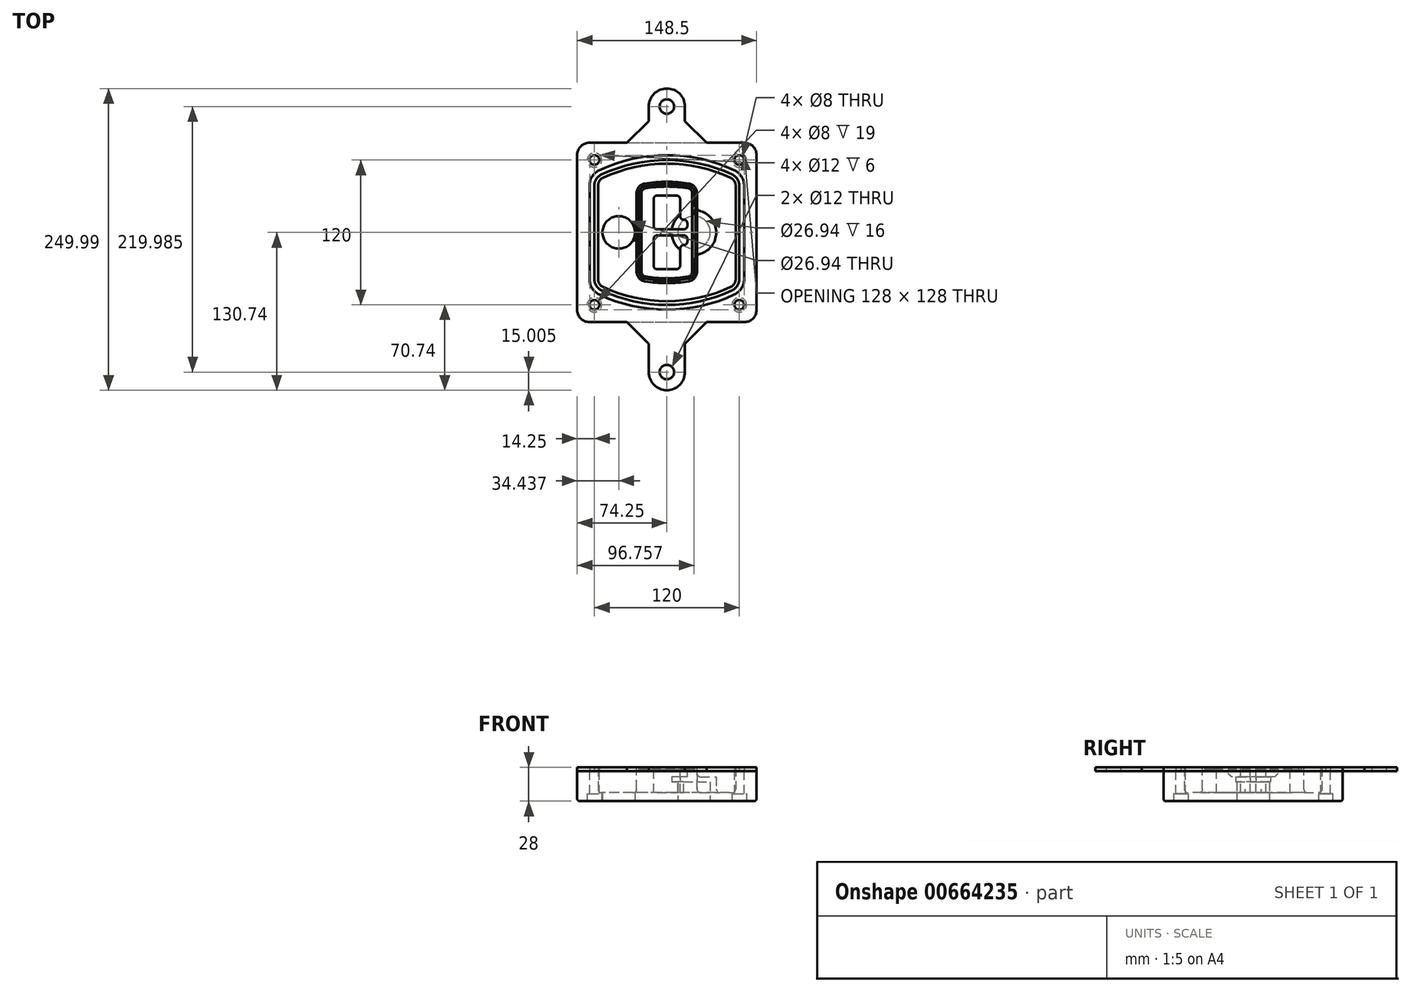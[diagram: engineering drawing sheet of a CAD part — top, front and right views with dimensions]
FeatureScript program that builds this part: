
annotation { "Feature Type Name" : "Feature", "Feature Type Description" : "" }
export const myFeature = defineFeature(function(context is Context, id is Id, definition is map)
    precondition{}
    {
        {
            var Q0;
            Q0=qCreatedBy(makeId("Top.planeOp"),FACE);
            var sketch = newSketch(context, id + "F0", { "sketchPlane" : qUnion([Q0])});
            skPoint(sketch, "E0.rect.middle", {"position": v(0, 0) * mm});
            skLineSegment(sketch, "E1.bottom", {"start": v(-64.25, -74.25) * mm, "end": v(64.25, -74.25) * mm});
            skLineSegment(sketch, "E1.top", {"start": v(-64.25, 74.25) * mm, "end": v(64.25, 74.25) * mm});
            skLineSegment(sketch, "E1.left", {"start": v(-74.25, -64.25) * mm, "end": v(-74.25, 64.25) * mm});
            skLineSegment(sketch, "E1.right", {"start": v(74.25, -64.25) * mm, "end": v(74.25, 64.25) * mm});
            skLineSegment(sketch, "E2", {"start": v(-74.25, 74.25) * mm, "end": v(74.25, -74.25) * mm, "construction": true});
            skLineSegment(sketch, "E3", {"start": v(74.25, 74.25) * mm, "end": v(-74.25, -74.25) * mm, "construction": true});
            skCircle(sketch, "E4", {"center": v(-60, 60) * mm, "radius": 4 * mm});
            skCircle(sketch, "E5", {"center": v(60, 60) * mm, "radius": 4 * mm});
            skCircle(sketch, "E6", {"center": v(60, -60) * mm, "radius": 4 * mm});
            skCircle(sketch, "E7", {"center": v(-60, -60) * mm, "radius": 4 * mm});
            skLineSegment(sketch, "E8", {"start": v(-60, 60) * mm, "end": v(60, 60) * mm, "construction": true});
            skLineSegment(sketch, "E9", {"start": v(60, 60) * mm, "end": v(60, -60) * mm, "construction": true});
            skLineSegment(sketch, "E10", {"start": v(60, -60) * mm, "end": v(-60, -60) * mm, "construction": true});
            skLineSegment(sketch, "E11", {"start": v(-60, -60) * mm, "end": v(-60, 60) * mm, "construction": true});
            skLineSegment(sketch, "E12", {"start": v(-60, 38.83) * mm, "end": v(-60, -38.83) * mm});
            skLineSegment(sketch, "E13", {"start": v(60, 38.83) * mm, "end": v(60, -38.83) * mm});
            skArc(sketch, "E14", {"start": v(54.26, 47.88) * mm, "mid": v(0, 60) * mm, "end": v(-54.26, 47.88) * mm});
            skArc(sketch, "E15", {"start": v(-54.26, -47.88) * mm, "mid": v(0, -60) * mm, "end": v(54.26, -47.88) * mm});
            skLineSegment(sketch, "E16", {"start": v(-60, 0) * mm, "end": v(60, 0) * mm, "construction": true});
            skPoint(sketch, "E17.visualSharp", {"position": v(-60, -45) * mm});
            skArc(sketch, "E17.filletArc", {"start": v(-60, -38.83) * mm, "mid": v(-58.44, -44.2) * mm, "end": v(-54.26, -47.88) * mm});
            skPoint(sketch, "E18.visualSharp", {"position": v(-60, 45) * mm});
            skArc(sketch, "E18.filletArc", {"start": v(-54.26, 47.88) * mm, "mid": v(-58.44, 44.2) * mm, "end": v(-60, 38.83) * mm});
            skPoint(sketch, "E19.visualSharp", {"position": v(60, 45) * mm});
            skArc(sketch, "E19.filletArc", {"start": v(60, 38.83) * mm, "mid": v(58.44, 44.2) * mm, "end": v(54.26, 47.88) * mm});
            skPoint(sketch, "E20.visualSharp", {"position": v(60, -45) * mm});
            skArc(sketch, "E20.filletArc", {"start": v(54.26, -47.88) * mm, "mid": v(58.44, -44.2) * mm, "end": v(60, -38.83) * mm});
            skPoint(sketch, "E21.visualSharp", {"position": v(-74.25, 74.25) * mm});
            skArc(sketch, "E21.filletArc", {"start": v(-64.25, 74.25) * mm, "mid": v(-71.32, 71.32) * mm, "end": v(-74.25, 64.25) * mm});
            skPoint(sketch, "E22.visualSharp", {"position": v(74.25, 74.25) * mm});
            skArc(sketch, "E22.filletArc", {"start": v(74.25, 64.25) * mm, "mid": v(71.32, 71.32) * mm, "end": v(64.25, 74.25) * mm});
            skPoint(sketch, "E23.visualSharp", {"position": v(74.25, -74.25) * mm});
            skArc(sketch, "E23.filletArc", {"start": v(64.25, -74.25) * mm, "mid": v(71.32, -71.32) * mm, "end": v(74.25, -64.25) * mm});
            skPoint(sketch, "E24.visualSharp", {"position": v(-74.25, -74.25) * mm});
            skArc(sketch, "E24.filletArc", {"start": v(-74.25, -64.25) * mm, "mid": v(-71.32, -71.32) * mm, "end": v(-64.25, -74.25) * mm});
            skArc(sketch, "E25.0", {"start": v(57, 38.83) * mm, "mid": v(55.9, 42.58) * mm, "end": v(52.98, 45.17) * mm});
            skLineSegment(sketch, "E25.1", {"start": v(57, 38.83) * mm, "end": v(57, -38.83) * mm});
            skArc(sketch, "E25.2", {"start": v(52.98, -45.17) * mm, "mid": v(55.9, -42.58) * mm, "end": v(57, -38.83) * mm});
            skArc(sketch, "E25.3", {"start": v(-52.98, -45.17) * mm, "mid": v(0, -57) * mm, "end": v(52.98, -45.17) * mm});
            skArc(sketch, "E25.4", {"start": v(-57, -38.83) * mm, "mid": v(-55.9, -42.58) * mm, "end": v(-52.98, -45.17) * mm});
            skArc(sketch, "E25.5", {"start": v(52.98, 45.17) * mm, "mid": v(0, 57) * mm, "end": v(-52.98, 45.17) * mm});
            skLineSegment(sketch, "E25.6", {"start": v(-57, 38.83) * mm, "end": v(-57, -38.83) * mm});
            skArc(sketch, "E25.7", {"start": v(-52.98, 45.17) * mm, "mid": v(-55.9, 42.58) * mm, "end": v(-57, 38.83) * mm});
            skArc(sketch, "E26.0", {"start": v(-55.96, 51.5) * mm, "mid": v(-61.82, 46.33) * mm, "end": v(-64, 38.83) * mm});
            skArc(sketch, "E26.1", {"start": v(55.96, 51.5) * mm, "mid": v(0, 64) * mm, "end": v(-55.96, 51.5) * mm});
            skArc(sketch, "E26.2", {"start": v(64, 38.83) * mm, "mid": v(61.82, 46.33) * mm, "end": v(55.96, 51.5) * mm});
            skLineSegment(sketch, "E26.3", {"start": v(64, 38.83) * mm, "end": v(64, -38.83) * mm});
            skArc(sketch, "E26.4", {"start": v(55.96, -51.5) * mm, "mid": v(61.82, -46.33) * mm, "end": v(64, -38.83) * mm});
            skLineSegment(sketch, "E26.5", {"start": v(-64, 38.83) * mm, "end": v(-64, -38.83) * mm});
            skArc(sketch, "E26.6", {"start": v(-55.96, -51.5) * mm, "mid": v(0, -64) * mm, "end": v(55.96, -51.5) * mm});
            skArc(sketch, "E26.7", {"start": v(-64, -38.83) * mm, "mid": v(-61.82, -46.33) * mm, "end": v(-55.96, -51.5) * mm});
            skLineSegment(sketch, "E27", {"start": v(0, 74.25) * mm, "end": v(0, 104.25) * mm, "construction": true});
            skCircle(sketch, "E28", {"center": v(0, 104.25) * mm, "radius": 6 * mm});
            skArc(sketch, "E29", {"start": v(-15, 104.25) * mm, "mid": v(0, 119.25) * mm, "end": v(15, 104.25) * mm});
            skLineSegment(sketch, "E30", {"start": v(-15, 104.25) * mm, "end": v(-15, 92.25) * mm});
            skLineSegment(sketch, "E31", {"start": v(15, 104.25) * mm, "end": v(15, 92.25) * mm});
            skLineSegment(sketch, "E32", {"start": v(15, 92.25) * mm, "end": v(33, 74.25) * mm});
            skLineSegment(sketch, "E33", {"start": v(-15, 92.25) * mm, "end": v(-33, 74.25) * mm});
            skArc(sketch, "E34.MirrorCS", {"start": v(15, 104.25) * mm, "mid": v(0, 119.25) * mm, "end": v(-15, 104.25) * mm});
            skLineSegment(sketch, "E35", {"start": v(-33, -74.25) * mm, "end": v(-15, -92.25) * mm});
            skLineSegment(sketch, "E36", {"start": v(33, -74.25) * mm, "end": v(15, -92.25) * mm});
            skLineSegment(sketch, "E37", {"start": v(-15, -92.25) * mm, "end": v(-15, -115.74) * mm});
            skLineSegment(sketch, "E38", {"start": v(15, -92.25) * mm, "end": v(15, -115.74) * mm});
            skCircle(sketch, "E39", {"center": v(0, -115.74) * mm, "radius": 6 * mm});
            skArc(sketch, "E40", {"start": v(-15, -115.74) * mm, "mid": v(0, -130.74) * mm, "end": v(15, -115.74) * mm});
            skSolve(sketch);
        }
        {
            var Q0;
            Q0=makeQuery(id+"F0.imprint","IMPRINT",FACE,{"disambiguationData":[TD([[makeQuery(id+"F0.imprint","IMPRINT",EDGE,{"derivedFrom":sQuery(id+"F0.wireOp",EDGE,"E1.bottom")}),1.0]])]});
            var Q1;
            Q1=makeQuery(id+"F0.imprint","IMPRINT",FACE,{"disambiguationData":[TD([[makeQuery(id+"F0.imprint","IMPRINT",EDGE,{"derivedFrom":sQuery(id+"F0.wireOp",EDGE,"E12")}),1.0]])]});
            var Q2;
            Q2=makeQuery(id+"F0.imprint","IMPRINT",FACE,{"disambiguationData":[TD([[makeQuery(id+"F0.imprint","IMPRINT",EDGE,{"derivedFrom":sQuery(id+"F0.wireOp",EDGE,"E25.0")}),1.0]])]});
            var Q3;
            Q3=makeQuery(id+"F0.imprint","IMPRINT",FACE,{"disambiguationData":[TD([[makeQuery(id+"F0.imprint","IMPRINT",EDGE,{"derivedFrom":sQuery(id+"F0.wireOp",EDGE,"E12")}),-1.0]])]});
            extrude(context, id + "F1", {"entities" : qUnion([Q0, Q1, Q2, Q3]), "oppositeDirection" : true, "depth" : 25 * mm});
        }
        {
            var Q0;
            Q0=makeQuery(id+"F0.imprint","IMPRINT",FACE,{"disambiguationData":[TD([[makeQuery(id+"F0.imprint","IMPRINT",EDGE,{"derivedFrom":sQuery(id+"F0.wireOp",EDGE,"E12")}),1.0]])]});
            extrude(context, id + "F2", {"entities" : qUnion([Q0]), "operationType" : NewBodyOperationType.ADD, "depth" : 3 * mm});
        }
        {
            var Q0;
            Q0=makeQuery(id+"F0.imprint","IMPRINT",FACE,{"disambiguationData":[TD([[makeQuery(id+"F0.imprint","IMPRINT",EDGE,{"derivedFrom":sQuery(id+"F0.wireOp",EDGE,"E25.0")}),1.0]])]});
            extrude(context, id + "F3", {"entities" : qUnion([Q0]), "operationType" : NewBodyOperationType.REMOVE, "oppositeDirection" : true, "depth" : 18 * mm});
        }
        {
            var Q0;
            Q0=makeQuery(id+"F2.opExtrude","CAP_FACE",FACE,{"disambiguationData":[OSD([sQuery(id+"F0.wireOp",EDGE,"E12"),sQuery(id+"F0.wireOp",EDGE,"E13"),sQuery(id+"F0.wireOp",EDGE,"E14"),sQuery(id+"F0.wireOp",EDGE,"E15"),sQuery(id+"F0.wireOp",EDGE,"E17.filletArc"),sQuery(id+"F0.wireOp",EDGE,"E18.filletArc"),sQuery(id+"F0.wireOp",EDGE,"E19.filletArc"),sQuery(id+"F0.wireOp",EDGE,"E20.filletArc"),sQuery(id+"F0.wireOp",EDGE,"E25.0"),sQuery(id+"F0.wireOp",EDGE,"E25.1"),sQuery(id+"F0.wireOp",EDGE,"E25.2"),sQuery(id+"F0.wireOp",EDGE,"E25.3"),sQuery(id+"F0.wireOp",EDGE,"E25.4"),sQuery(id+"F0.wireOp",EDGE,"E25.5"),sQuery(id+"F0.wireOp",EDGE,"E25.6"),sQuery(id+"F0.wireOp",EDGE,"E25.7")])],"isStart":false});
            var sketch = newSketch(context, id + "F4", { "sketchPlane" : qUnion([Q0])});
            skArc(sketch, "E41.0", {"start": v(-18.34, -40.45) * mm, "mid": v(0, -42) * mm, "end": v(18.34, -40.45) * mm});
            skArc(sketch, "E42.0", {"start": v(18.34, 40.45) * mm, "mid": v(0, 42) * mm, "end": v(-18.34, 40.45) * mm});
            skLineSegment(sketch, "E43", {"start": v(-25, 32.57) * mm, "end": v(-25, -32.57) * mm});
            skLineSegment(sketch, "E44", {"start": v(25, 32.57) * mm, "end": v(25, -32.57) * mm});
            skLineSegment(sketch, "E45", {"start": v(-25, 39.1) * mm, "end": v(25, 39.1) * mm, "construction": true});
            skLineSegment(sketch, "E46", {"start": v(-25, -39.1) * mm, "end": v(25, -39.1) * mm, "construction": true});
            skPoint(sketch, "E47.visualSharp", {"position": v(-25, 39.1) * mm});
            skArc(sketch, "E47.filletArc", {"start": v(-18.34, 40.45) * mm, "mid": v(-23.11, 37.73) * mm, "end": v(-25, 32.57) * mm});
            skPoint(sketch, "E48.visualSharp", {"position": v(25, 39.1) * mm});
            skArc(sketch, "E48.filletArc", {"start": v(25, 32.57) * mm, "mid": v(23.11, 37.73) * mm, "end": v(18.34, 40.45) * mm});
            skPoint(sketch, "E49.visualSharp", {"position": v(25, -39.1) * mm});
            skArc(sketch, "E49.filletArc", {"start": v(18.34, -40.45) * mm, "mid": v(23.11, -37.73) * mm, "end": v(25, -32.57) * mm});
            skPoint(sketch, "E50.visualSharp", {"position": v(-25, -39.1) * mm});
            skArc(sketch, "E50.filletArc", {"start": v(-25, -32.57) * mm, "mid": v(-23.11, -37.73) * mm, "end": v(-18.34, -40.45) * mm});
            skArc(sketch, "E51.0", {"start": v(52.98, 45.17) * mm, "mid": v(0, 57) * mm, "end": v(-52.98, 45.17) * mm});
            skArc(sketch, "E51.1", {"start": v(-52.98, 45.17) * mm, "mid": v(-55.9, 42.58) * mm, "end": v(-57, 38.83) * mm});
            skLineSegment(sketch, "E51.2", {"start": v(-57, 38.83) * mm, "end": v(-57, -38.83) * mm});
            skArc(sketch, "E51.3", {"start": v(-57, -38.83) * mm, "mid": v(-55.9, -42.58) * mm, "end": v(-52.98, -45.17) * mm});
            skArc(sketch, "E51.4", {"start": v(-52.98, -45.17) * mm, "mid": v(0, -57) * mm, "end": v(52.98, -45.17) * mm});
            skArc(sketch, "E51.5", {"start": v(52.98, -45.17) * mm, "mid": v(55.9, -42.58) * mm, "end": v(57, -38.83) * mm});
            skLineSegment(sketch, "E51.6", {"start": v(57, 38.83) * mm, "end": v(57, -38.83) * mm});
            skArc(sketch, "E51.7", {"start": v(57, 38.83) * mm, "mid": v(55.9, 42.58) * mm, "end": v(52.98, 45.17) * mm});
            skLineSegment(sketch, "E52.0", {"start": v(23, 32.57) * mm, "end": v(23, -32.57) * mm});
            skArc(sketch, "E52.1", {"start": v(18, -38.48) * mm, "mid": v(21.58, -36.44) * mm, "end": v(23, -32.57) * mm});
            skArc(sketch, "E52.2", {"start": v(-18, -38.48) * mm, "mid": v(0, -40) * mm, "end": v(18, -38.48) * mm});
            skArc(sketch, "E52.3", {"start": v(-23, -32.57) * mm, "mid": v(-21.58, -36.44) * mm, "end": v(-18, -38.48) * mm});
            skLineSegment(sketch, "E52.4", {"start": v(-23, 32.57) * mm, "end": v(-23, -32.57) * mm});
            skArc(sketch, "E52.5", {"start": v(23, 32.57) * mm, "mid": v(21.58, 36.44) * mm, "end": v(18, 38.48) * mm});
            skArc(sketch, "E52.6", {"start": v(-18, 38.48) * mm, "mid": v(-21.58, 36.44) * mm, "end": v(-23, 32.57) * mm});
            skArc(sketch, "E52.7", {"start": v(18, 38.48) * mm, "mid": v(0, 40) * mm, "end": v(-18, 38.48) * mm});
            skArc(sketch, "E53.0", {"start": v(21, 32.57) * mm, "mid": v(20.06, 35.15) * mm, "end": v(17.67, 36.5) * mm});
            skLineSegment(sketch, "E53.1", {"start": v(21, 32.57) * mm, "end": v(21, -32.57) * mm});
            skArc(sketch, "E53.2", {"start": v(17.67, -36.5) * mm, "mid": v(20.06, -35.15) * mm, "end": v(21, -32.57) * mm});
            skArc(sketch, "E53.3", {"start": v(-17.67, -36.5) * mm, "mid": v(0, -38) * mm, "end": v(17.67, -36.5) * mm});
            skArc(sketch, "E53.4", {"start": v(-21, -32.57) * mm, "mid": v(-20.06, -35.15) * mm, "end": v(-17.67, -36.5) * mm});
            skArc(sketch, "E53.5", {"start": v(17.67, 36.5) * mm, "mid": v(0, 38) * mm, "end": v(-17.67, 36.5) * mm});
            skLineSegment(sketch, "E53.6", {"start": v(-21, 32.57) * mm, "end": v(-21, -32.57) * mm});
            skArc(sketch, "E53.7", {"start": v(-17.67, 36.5) * mm, "mid": v(-20.06, 35.15) * mm, "end": v(-21, 32.57) * mm});
            skLineSegment(sketch, "E54", {"start": v(-25, 0) * mm, "end": v(25, 0) * mm, "construction": true});
            skLineSegment(sketch, "E55", {"start": v(-11, 5.5) * mm, "end": v(-11, 27.5) * mm});
            skLineSegment(sketch, "E56", {"start": v(-8, 30.5) * mm, "end": v(8, 30.5) * mm});
            skLineSegment(sketch, "E57", {"start": v(11, 27.5) * mm, "end": v(11, 13.5) * mm});
            skLineSegment(sketch, "E58", {"start": v(14, 10.5) * mm, "end": v(14, 10.5) * mm});
            skLineSegment(sketch, "E59", {"start": v(17, 7.5) * mm, "end": v(17, 5.5) * mm});
            skLineSegment(sketch, "E60", {"start": v(14, 2.5) * mm, "end": v(-8, 2.5) * mm});
            skPoint(sketch, "E61.visualSharp", {"position": v(-11, 30.5) * mm});
            skArc(sketch, "E61.filletArc", {"start": v(-8, 30.5) * mm, "mid": v(-10.12, 29.62) * mm, "end": v(-11, 27.5) * mm});
            skPoint(sketch, "E62.visualSharp", {"position": v(11, 30.5) * mm});
            skArc(sketch, "E62.filletArc", {"start": v(11, 27.5) * mm, "mid": v(10.12, 29.62) * mm, "end": v(8, 30.5) * mm});
            skPoint(sketch, "E63.visualSharp", {"position": v(11, 10.5) * mm});
            skArc(sketch, "E63.filletArc", {"start": v(11, 13.5) * mm, "mid": v(11.88, 11.38) * mm, "end": v(14, 10.5) * mm});
            skPoint(sketch, "E64.visualSharp", {"position": v(17, 10.5) * mm});
            skArc(sketch, "E64.filletArc", {"start": v(17, 7.5) * mm, "mid": v(16.12, 9.62) * mm, "end": v(14, 10.5) * mm});
            skPoint(sketch, "E65.visualSharp", {"position": v(17, 2.5) * mm});
            skArc(sketch, "E65.filletArc", {"start": v(14, 2.5) * mm, "mid": v(16.12, 3.38) * mm, "end": v(17, 5.5) * mm});
            skPoint(sketch, "E66.visualSharp", {"position": v(-11, 2.5) * mm});
            skArc(sketch, "E66.filletArc", {"start": v(-11, 5.5) * mm, "mid": v(-10.12, 3.38) * mm, "end": v(-8, 2.5) * mm});
            skLineSegment(sketch, "E67.0.MirrorCS", {"start": v(14, -2.5) * mm, "end": v(-8, -2.5) * mm});
            skArc(sketch, "E68.0.MirrorCS", {"start": v(-11, -5.5) * mm, "mid": v(-10.12, -3.38) * mm, "end": v(-8, -2.5) * mm});
            skLineSegment(sketch, "E69.0.MirrorCS", {"start": v(-11, -5.5) * mm, "end": v(-11, -27.5) * mm});
            skArc(sketch, "E70.0.MirrorCS", {"start": v(-8, -30.5) * mm, "mid": v(-10.12, -29.62) * mm, "end": v(-11, -27.5) * mm});
            skLineSegment(sketch, "E71.0.MirrorCS", {"start": v(-8, -30.5) * mm, "end": v(8, -30.5) * mm});
            skArc(sketch, "E72.0.MirrorCS", {"start": v(11, -27.5) * mm, "mid": v(10.12, -29.62) * mm, "end": v(8, -30.5) * mm});
            skLineSegment(sketch, "E73.0.MirrorCS", {"start": v(11, -27.5) * mm, "end": v(11, -13.5) * mm});
            skArc(sketch, "E74.0.MirrorCS", {"start": v(11, -13.5) * mm, "mid": v(11.88, -11.38) * mm, "end": v(14, -10.5) * mm});
            skArc(sketch, "E75.0.MirrorCS", {"start": v(17, -7.5) * mm, "mid": v(16.12, -9.62) * mm, "end": v(14, -10.5) * mm});
            skLineSegment(sketch, "E76.0.MirrorCS", {"start": v(17, -7.5) * mm, "end": v(17, -5.5) * mm});
            skArc(sketch, "E77.0.MirrorCS", {"start": v(14, -2.5) * mm, "mid": v(16.12, -3.38) * mm, "end": v(17, -5.5) * mm});
            skSolve(sketch);
        }
        {
            var Q0;
            Q0=makeQuery(id+"F4.imprint","IMPRINT",FACE,{"disambiguationData":[TD([[makeQuery(id+"F4.imprint","IMPRINT",EDGE,{"derivedFrom":sQuery(id+"F4.wireOp",EDGE,"E41.0")}),1.0]])]});
            var Q1;
            Q1=makeQuery(id+"F4.imprint","IMPRINT",FACE,{"disambiguationData":[TD([[makeQuery(id+"F4.imprint","IMPRINT",EDGE,{"derivedFrom":sQuery(id+"F4.wireOp",EDGE,"E52.0")}),-1.0]])]});
            var Q2;
            Q2=makeQuery(id+"F4.imprint","IMPRINT",FACE,{"disambiguationData":[TD([[makeQuery(id+"F4.imprint","IMPRINT",EDGE,{"derivedFrom":sQuery(id+"F4.wireOp",EDGE,"E53.0")}),1.0]])]});
            extrude(context, id + "F5", {"entities" : qUnion([Q0, Q1, Q2]), "operationType" : NewBodyOperationType.ADD, "endBound" : BoundingType.UP_TO_NEXT, "oppositeDirection" : true, "depth" : 25 * mm});
        }
        {
            var Q0;
            Q0=makeQuery(id+"F4.imprint","IMPRINT",FACE,{"disambiguationData":[TD([[makeQuery(id+"F4.imprint","IMPRINT",EDGE,{"derivedFrom":sQuery(id+"F4.wireOp",EDGE,"E52.0")}),-1.0]])]});
            extrude(context, id + "F6", {"entities" : qUnion([Q0]), "operationType" : NewBodyOperationType.REMOVE, "oppositeDirection" : true, "depth" : 2 * mm});
        }
        {
            var Q0;
            Q0=makeQuery(id+"F1.opExtrude","CAP_FACE",FACE,{"disambiguationData":[OSD([sQuery(id+"F0.wireOp",EDGE,"E1.bottom"),sQuery(id+"F0.wireOp",EDGE,"E1.top"),sQuery(id+"F0.wireOp",EDGE,"E1.left"),sQuery(id+"F0.wireOp",EDGE,"E1.right"),sQuery(id+"F0.wireOp",EDGE,"E4"),sQuery(id+"F0.wireOp",EDGE,"E5"),sQuery(id+"F0.wireOp",EDGE,"E6"),sQuery(id+"F0.wireOp",EDGE,"E7"),sQuery(id+"F0.wireOp",EDGE,"E21.filletArc"),sQuery(id+"F0.wireOp",EDGE,"E22.filletArc"),sQuery(id+"F0.wireOp",EDGE,"E23.filletArc"),sQuery(id+"F0.wireOp",EDGE,"E24.filletArc")])],"isStart":false});
            var sketch = newSketch(context, id + "F7", { "sketchPlane" : qUnion([Q0])});
            skCircle(sketch, "E78", {"center": v(22.5, 0) * mm, "radius": 13.47 * mm});
            skCircle(sketch, "E79", {"center": v(-39.81, 0) * mm, "radius": 13.47 * mm});
            skLineSegment(sketch, "E80", {"start": v(74.25, 0) * mm, "end": v(-74.25, 0) * mm});
            skCircle(sketch, "E81", {"center": v(22.5, 0) * mm, "radius": 18.47 * mm});
            skCircle(sketch, "E82", {"center": v(60, -60) * mm, "radius": 6 * mm});
            skCircle(sketch, "E83", {"center": v(-60, -60) * mm, "radius": 6 * mm});
            skCircle(sketch, "E84", {"center": v(-60, 60) * mm, "radius": 6 * mm});
            skCircle(sketch, "E85", {"center": v(60, 60) * mm, "radius": 6 * mm});
            skSolve(sketch);
        }
        {
            var Q0;
            {var subQ1=sQuery(id+"F7.wireOp",EDGE,"E80");var subQ4=sQuery(id+"F7.wireOp",EDGE,"E78");var subQ6=makeQuery(id+"F7.imprint","INTERSECT",VERTEX,{"disambiguationData":[OD(0.0)],"derivedFrom":[subQ4,subQ1]});Q0=makeQuery(id+"F7.imprint","IMPRINT",FACE,{"disambiguationData":[TD([[makeQuery(id+"F7.imprint","IMPRINT",EDGE,{"disambiguationData":[TD([[subQ6,-1.0]])],"derivedFrom":subQ4}),-1.0]])]});}
            var Q1;
            {var subQ0=sQuery(id+"F7.wireOp",EDGE,"E80");var subQ1=sQuery(id+"F7.wireOp",EDGE,"E78");var subQ3=makeQuery(id+"F7.imprint","INTERSECT",VERTEX,{"disambiguationData":[OD(0.0)],"derivedFrom":[subQ1,subQ0]});Q1=makeQuery(id+"F7.imprint","IMPRINT",FACE,{"disambiguationData":[TD([[makeQuery(id+"F7.imprint","IMPRINT",EDGE,{"disambiguationData":[TD([[subQ3,-1.0]])],"derivedFrom":subQ1}),1.0]])]});}
            var Q2;
            {var subQ0=sQuery(id+"F7.wireOp",EDGE,"E80");var subQ1=sQuery(id+"F7.wireOp",EDGE,"E78");var subQ3=makeQuery(id+"F7.imprint","INTERSECT",VERTEX,{"disambiguationData":[OD(0.0)],"derivedFrom":[subQ1,subQ0]});Q2=makeQuery(id+"F7.imprint","IMPRINT",FACE,{"disambiguationData":[TD([[makeQuery(id+"F7.imprint","IMPRINT",EDGE,{"disambiguationData":[TD([[subQ3,1.0]])],"derivedFrom":subQ1}),1.0]])]});}
            var Q3;
            {var subQ1=sQuery(id+"F7.wireOp",EDGE,"E80");var subQ4=sQuery(id+"F7.wireOp",EDGE,"E78");var subQ6=makeQuery(id+"F7.imprint","INTERSECT",VERTEX,{"disambiguationData":[OD(0.0)],"derivedFrom":[subQ4,subQ1]});Q3=makeQuery(id+"F7.imprint","IMPRINT",FACE,{"disambiguationData":[TD([[makeQuery(id+"F7.imprint","IMPRINT",EDGE,{"disambiguationData":[TD([[subQ6,1.0]])],"derivedFrom":subQ4}),-1.0]])]});}
            extrude(context, id + "F8", {"entities" : qUnion([Q0, Q1, Q2, Q3]), "operationType" : NewBodyOperationType.ADD, "oppositeDirection" : true, "depth" : 20 * mm});
        }
        {
            var Q0;
            {var subQ0=sQuery(id+"F7.wireOp",EDGE,"E80");var subQ1=sQuery(id+"F7.wireOp",EDGE,"E78");var subQ3=makeQuery(id+"F7.imprint","INTERSECT",VERTEX,{"disambiguationData":[OD(0.0)],"derivedFrom":[subQ1,subQ0]});Q0=makeQuery(id+"F7.imprint","IMPRINT",FACE,{"disambiguationData":[TD([[makeQuery(id+"F7.imprint","IMPRINT",EDGE,{"disambiguationData":[TD([[subQ3,-1.0]])],"derivedFrom":subQ1}),1.0]])]});}
            var Q1;
            {var subQ0=sQuery(id+"F7.wireOp",EDGE,"E80");var subQ1=sQuery(id+"F7.wireOp",EDGE,"E78");var subQ3=makeQuery(id+"F7.imprint","INTERSECT",VERTEX,{"disambiguationData":[OD(0.0)],"derivedFrom":[subQ1,subQ0]});Q1=makeQuery(id+"F7.imprint","IMPRINT",FACE,{"disambiguationData":[TD([[makeQuery(id+"F7.imprint","IMPRINT",EDGE,{"disambiguationData":[TD([[subQ3,1.0]])],"derivedFrom":subQ1}),1.0]])]});}
            extrude(context, id + "F9", {"entities" : qUnion([Q0, Q1]), "operationType" : NewBodyOperationType.REMOVE, "oppositeDirection" : true, "depth" : 16 * mm});
        }
        {
            var Q0;
            {var subQ0=sQuery(id+"F7.wireOp",EDGE,"E80");var subQ1=sQuery(id+"F7.wireOp",EDGE,"E79");var subQ3=makeQuery(id+"F7.imprint","INTERSECT",VERTEX,{"disambiguationData":[OD(0.0)],"derivedFrom":[subQ1,subQ0]});Q0=makeQuery(id+"F7.imprint","IMPRINT",FACE,{"disambiguationData":[TD([[makeQuery(id+"F7.imprint","IMPRINT",EDGE,{"disambiguationData":[TD([[subQ3,-1.0]])],"derivedFrom":subQ1}),1.0]])]});}
            var Q1;
            {var subQ0=sQuery(id+"F7.wireOp",EDGE,"E80");var subQ1=sQuery(id+"F7.wireOp",EDGE,"E79");var subQ3=makeQuery(id+"F7.imprint","INTERSECT",VERTEX,{"disambiguationData":[OD(0.0)],"derivedFrom":[subQ1,subQ0]});Q1=makeQuery(id+"F7.imprint","IMPRINT",FACE,{"disambiguationData":[TD([[makeQuery(id+"F7.imprint","IMPRINT",EDGE,{"disambiguationData":[TD([[subQ3,1.0]])],"derivedFrom":subQ1}),1.0]])]});}
            extrude(context, id + "F10", {"entities" : qUnion([Q0, Q1]), "operationType" : NewBodyOperationType.REMOVE, "oppositeDirection" : true, "depth" : 25 * mm});
        }
        {
            var Q0;
            Q0=makeQuery(id+"F7.imprint","IMPRINT",FACE,{"disambiguationData":[TD([[makeQuery(id+"F7.imprint","IMPRINT",EDGE,{"derivedFrom":sQuery(id+"F7.wireOp",EDGE,"E82")}),1.0]])]});
            var Q1;
            Q1=makeQuery(id+"F7.imprint","IMPRINT",FACE,{"disambiguationData":[TD([[makeQuery(id+"F7.imprint","IMPRINT",EDGE,{"derivedFrom":makeQuery(id+"F1.opExtrude","CAP_EDGE",EDGE,{"disambiguationData":[OSD([sQuery(id+"F0.wireOp",EDGE,"E5")])],"isStart":false})}),-1.0]])]});
            var Q2;
            Q2=makeQuery(id+"F7.imprint","IMPRINT",FACE,{"disambiguationData":[TD([[makeQuery(id+"F7.imprint","IMPRINT",EDGE,{"derivedFrom":sQuery(id+"F7.wireOp",EDGE,"E83")}),1.0]])]});
            var Q3;
            Q3=makeQuery(id+"F7.imprint","IMPRINT",FACE,{"disambiguationData":[TD([[makeQuery(id+"F7.imprint","IMPRINT",EDGE,{"derivedFrom":makeQuery(id+"F1.opExtrude","CAP_EDGE",EDGE,{"disambiguationData":[OSD([sQuery(id+"F0.wireOp",EDGE,"E4")])],"isStart":false})}),-1.0]])]});
            var Q4;
            Q4=makeQuery(id+"F7.imprint","IMPRINT",FACE,{"disambiguationData":[TD([[makeQuery(id+"F7.imprint","IMPRINT",EDGE,{"derivedFrom":sQuery(id+"F7.wireOp",EDGE,"E84")}),1.0]])]});
            var Q5;
            Q5=makeQuery(id+"F7.imprint","IMPRINT",FACE,{"disambiguationData":[TD([[makeQuery(id+"F7.imprint","IMPRINT",EDGE,{"derivedFrom":makeQuery(id+"F1.opExtrude","CAP_EDGE",EDGE,{"disambiguationData":[OSD([sQuery(id+"F0.wireOp",EDGE,"E7")])],"isStart":false})}),-1.0]])]});
            var Q6;
            Q6=makeQuery(id+"F7.imprint","IMPRINT",FACE,{"disambiguationData":[TD([[makeQuery(id+"F7.imprint","IMPRINT",EDGE,{"derivedFrom":sQuery(id+"F7.wireOp",EDGE,"E85")}),1.0]])]});
            var Q7;
            Q7=makeQuery(id+"F7.imprint","IMPRINT",FACE,{"disambiguationData":[TD([[makeQuery(id+"F7.imprint","IMPRINT",EDGE,{"derivedFrom":makeQuery(id+"F1.opExtrude","CAP_EDGE",EDGE,{"disambiguationData":[OSD([sQuery(id+"F0.wireOp",EDGE,"E6")])],"isStart":false})}),-1.0]])]});
            extrude(context, id + "F11", {"entities" : qUnion([Q0, Q1, Q2, Q3, Q4, Q5, Q6, Q7]), "operationType" : NewBodyOperationType.REMOVE, "oppositeDirection" : true, "depth" : 6 * mm});
        }
        {
            var Q0;
            Q0=makeQuery(id+"F9.boolean.opBoolean","COPY",FACE,{"derivedFrom":makeQuery(id+"F9.opExtrude","CAP_FACE",FACE,{"disambiguationData":[OSD([sQuery(id+"F7.wireOp",EDGE,"E78")])],"isStart":false})});
            var sketch = newSketch(context, id + "F12", { "sketchPlane" : qUnion([Q0])});
            skArc(sketch, "E86.0", {"start": v(11, 14.45) * mm, "mid": v(6.45, 9.13) * mm, "end": v(4.2, 2.5) * mm});
            skArc(sketch, "E86.1", {"start": v(4.2, -2.5) * mm, "mid": v(6.45, -9.13) * mm, "end": v(11, -14.45) * mm});
            skLineSegment(sketch, "E87", {"start": v(4.2, -2.5) * mm, "end": v(14, -2.5) * mm});
            skLineSegment(sketch, "E88.0", {"start": v(14, 2.5) * mm, "end": v(4.2, 2.5) * mm});
            skArc(sketch, "E88.1", {"start": v(14, 2.5) * mm, "mid": v(16.12, 3.38) * mm, "end": v(17, 5.5) * mm});
            skLineSegment(sketch, "E88.2", {"start": v(17, 7.5) * mm, "end": v(17, 5.5) * mm});
            skArc(sketch, "E88.3", {"start": v(17, 7.5) * mm, "mid": v(16.12, 9.62) * mm, "end": v(14, 10.5) * mm});
            skArc(sketch, "E88.4", {"start": v(11, 13.5) * mm, "mid": v(11.88, 11.38) * mm, "end": v(14, 10.5) * mm});
            skLineSegment(sketch, "E88.5", {"start": v(11, 14.45) * mm, "end": v(11, 13.5) * mm});
            skLineSegment(sketch, "E88.7", {"start": v(14, -2.5) * mm, "end": v(4.2, -2.5) * mm});
            skArc(sketch, "E88.8", {"start": v(14, -2.5) * mm, "mid": v(16.12, -3.38) * mm, "end": v(17, -5.5) * mm});
            skLineSegment(sketch, "E88.9", {"start": v(17, -7.5) * mm, "end": v(17, -5.5) * mm});
            skArc(sketch, "E88.10", {"start": v(17, -7.5) * mm, "mid": v(16.12, -9.62) * mm, "end": v(14, -10.5) * mm});
            skArc(sketch, "E88.11", {"start": v(11, -13.5) * mm, "mid": v(11.88, -11.38) * mm, "end": v(14, -10.5) * mm});
            skLineSegment(sketch, "E88.12", {"start": v(11, -14.45) * mm, "end": v(11, -13.5) * mm});
            skPoint(sketch, "E89.orphan", {"position": v(11, -27.5) * mm});
            skPoint(sketch, "E90.orphan", {"position": v(-8, -2.5) * mm});
            skPoint(sketch, "E91.orphan", {"position": v(-8, 2.5) * mm});
            skPoint(sketch, "E92.orphan", {"position": v(11, 27.5) * mm});
            skSolve(sketch);
        }
        {
            var Q0;
            {var subQ7=sQuery(id+"F12.wireOp",EDGE,"E86.0");var subQ14=sQuery(id+"F12.wireOp",EDGE,"E86.1");var subQ16=sQuery(id+"F12.wireOp",EDGE,"E88.1");var subQ18=sQuery(id+"F12.wireOp",EDGE,"E88.8");Q0=qUnion([makeQuery(id+"F12.imprint","IMPRINT",FACE,{"disambiguationData":[TD([[makeQuery(id+"F12.imprint","IMPRINT",EDGE,{"derivedFrom":subQ7}),1.0]])]}),makeQuery(id+"F12.imprint","IMPRINT",FACE,{"disambiguationData":[TD([[makeQuery(id+"F12.imprint","IMPRINT",EDGE,{"derivedFrom":subQ14}),1.0]])]}),makeQuery(id+"F12.imprint","IMPRINT",FACE,{"disambiguationData":[TD([[makeQuery(id+"F12.imprint","IMPRINT",EDGE,{"derivedFrom":subQ16}),1.0]])]}),makeQuery(id+"F12.imprint","IMPRINT",FACE,{"disambiguationData":[TD([[makeQuery(id+"F12.imprint","IMPRINT",EDGE,{"derivedFrom":subQ18}),-1.0]])]})]);}
            var Q1;
            Q1=makeQuery(id+"F5.boolean.opBoolean","SPLIT",FACE,{"disambiguationData":[TD([makeQuery(id+"F5.opExtrude","SWEPT_FACE",FACE,{"disambiguationData":[OSD([sQuery(id+"F4.wireOp",EDGE,"E55")])]})])],"derivedFrom":makeQuery(id+"F3.boolean.opBoolean","COPY",FACE,{"derivedFrom":makeQuery(id+"F3.opExtrude","CAP_FACE",FACE,{"disambiguationData":[OSD([sQuery(id+"F0.wireOp",EDGE,"E25.0"),sQuery(id+"F0.wireOp",EDGE,"E25.1"),sQuery(id+"F0.wireOp",EDGE,"E25.2"),sQuery(id+"F0.wireOp",EDGE,"E25.3"),sQuery(id+"F0.wireOp",EDGE,"E25.4"),sQuery(id+"F0.wireOp",EDGE,"E25.5"),sQuery(id+"F0.wireOp",EDGE,"E25.6"),sQuery(id+"F0.wireOp",EDGE,"E25.7")])],"isStart":false})})});
            extrude(context, id + "F13", {"entities" : qUnion([Q0]), "operationType" : NewBodyOperationType.REMOVE, "endBound" : BoundingType.UP_TO_SURFACE, "endBoundEntityFace" : qUnion([Q1]), "depth" : 25 * mm});
        }
        {
            var Q0;
            Q0=makeQuery(id+"F3.boolean.opBoolean","COPY",EDGE,{"derivedFrom":makeQuery(id+"F3.opExtrude","CAP_EDGE",EDGE,{"disambiguationData":[OSD([sQuery(id+"F0.wireOp",EDGE,"E25.6")])],"isStart":false})});
            var Q1;
            Q1=makeQuery(id+"F8.boolean.opBoolean","INTERSECT",EDGE,{"derivedFrom":[makeQuery(id+"F5.opExtrude","SWEPT_FACE",FACE,{"disambiguationData":[OSD([sQuery(id+"F4.wireOp",EDGE,"E44")])]}),makeQuery(id+"F8.opExtrude","CAP_FACE",FACE,{"disambiguationData":[OSD([sQuery(id+"F7.wireOp",EDGE,"E81")])],"isStart":false})]});
            var Q2;
            Q2=makeQuery(id+"F8.boolean.opBoolean","INTERSECT",EDGE,{"disambiguationData":[OD(1.0)],"derivedFrom":[makeQuery(id+"F5.opExtrude","SWEPT_FACE",FACE,{"disambiguationData":[OSD([sQuery(id+"F4.wireOp",EDGE,"E44")])]}),makeQuery(id+"F8.opExtrude","SWEPT_FACE",FACE,{"disambiguationData":[OSD([sQuery(id+"F7.wireOp",EDGE,"E81")])]})]});
            var Q3;
            {var subQ0=sQuery(id+"F4.wireOp",EDGE,"E44");Q3=makeQuery(id+"F8.boolean.opBoolean","SPLIT",EDGE,{"disambiguationData":[TD([makeQuery(id+"F5.opExtrude","SWEPT_FACE",FACE,{"disambiguationData":[OSD([sQuery(id+"F4.wireOp",EDGE,"E49.filletArc")])]})])],"derivedFrom":makeQuery(id+"F5.opExtrude","CAP_EDGE",EDGE,{"disambiguationData":[OSD([subQ0])],"isStart":false})});}
            var Q4;
            {var subQ0=sQuery(id+"F0.wireOp",EDGE,"E25.7");var subQ1=sQuery(id+"F0.wireOp",EDGE,"E25.1");var subQ2=sQuery(id+"F0.wireOp",EDGE,"E25.6");var subQ3=sQuery(id+"F0.wireOp",EDGE,"E25.5");var subQ4=sQuery(id+"F0.wireOp",EDGE,"E25.4");var subQ5=sQuery(id+"F0.wireOp",EDGE,"E25.0");var subQ6=sQuery(id+"F0.wireOp",EDGE,"E25.2");var subQ7=sQuery(id+"F0.wireOp",EDGE,"E25.3");Q4=makeQuery(id+"F8.boolean.opBoolean","INTERSECT",EDGE,{"derivedFrom":[makeQuery(id+"F5.boolean.opBoolean","SPLIT",FACE,{"disambiguationData":[TD([makeQuery(id+"F2.opExtrude","SWEPT_FACE",FACE,{"disambiguationData":[OSD([subQ5])]})])],"derivedFrom":makeQuery(id+"F3.boolean.opBoolean","COPY",FACE,{"derivedFrom":makeQuery(id+"F3.opExtrude","CAP_FACE",FACE,{"disambiguationData":[OSD([subQ5,subQ1,subQ6,subQ7,subQ4,subQ3,subQ2,subQ0])],"isStart":false})})}),makeQuery(id+"F8.opExtrude","SWEPT_FACE",FACE,{"disambiguationData":[OSD([sQuery(id+"F7.wireOp",EDGE,"E81")])]})]});}
            var Q5;
            Q5=makeQuery(id+"F8.boolean.opBoolean","INTERSECT",EDGE,{"disambiguationData":[OD(0.0)],"derivedFrom":[makeQuery(id+"F5.opExtrude","SWEPT_FACE",FACE,{"disambiguationData":[OSD([sQuery(id+"F4.wireOp",EDGE,"E44")])]}),makeQuery(id+"F8.opExtrude","SWEPT_FACE",FACE,{"disambiguationData":[OSD([sQuery(id+"F7.wireOp",EDGE,"E81")])]})]});
            fillet(context, id + "F14", {"entities" : qUnion([Q0, Q1, Q2, Q3, Q4, Q5]), "radius" : 3 * mm, "tangentPropagation" : true, "allowEdgeOverflow" : false});
        }
        {
            var Q0;
            Q0=makeQuery(id+"F1.opExtrude","CAP_EDGE",EDGE,{"disambiguationData":[OSD([sQuery(id+"F0.wireOp",EDGE,"E1.bottom")])],"isStart":false});
            fillet(context, id + "F15", {"entities" : qUnion([Q0]), "radius" : 2 * mm, "tangentPropagation" : true, "allowEdgeOverflow" : false});
        }
        {
            var Q0;
            Q0 = qSketchRegion(id + "F0", true);
            var Q1;
            Q1=makeQuery(id+"F2.opExtrude","CAP_FACE",FACE,{"disambiguationData":[OSD([sQuery(id+"F0.wireOp",EDGE,"E12"),sQuery(id+"F0.wireOp",EDGE,"E13"),sQuery(id+"F0.wireOp",EDGE,"E14"),sQuery(id+"F0.wireOp",EDGE,"E15"),sQuery(id+"F0.wireOp",EDGE,"E17.filletArc"),sQuery(id+"F0.wireOp",EDGE,"E18.filletArc"),sQuery(id+"F0.wireOp",EDGE,"E19.filletArc"),sQuery(id+"F0.wireOp",EDGE,"E20.filletArc"),sQuery(id+"F0.wireOp",EDGE,"E25.0"),sQuery(id+"F0.wireOp",EDGE,"E25.1"),sQuery(id+"F0.wireOp",EDGE,"E25.2"),sQuery(id+"F0.wireOp",EDGE,"E25.3"),sQuery(id+"F0.wireOp",EDGE,"E25.4"),sQuery(id+"F0.wireOp",EDGE,"E25.5"),sQuery(id+"F0.wireOp",EDGE,"E25.6"),sQuery(id+"F0.wireOp",EDGE,"E25.7")])],"isStart":false});
            extrude(context, id + "F16", {"entities" : qUnion([Q0]), "endBound" : BoundingType.UP_TO_SURFACE, "depth" : 25 * mm, "endBoundEntityFace" : qUnion([Q1]), "offsetDistance" : 25 * mm});
        }
    });
